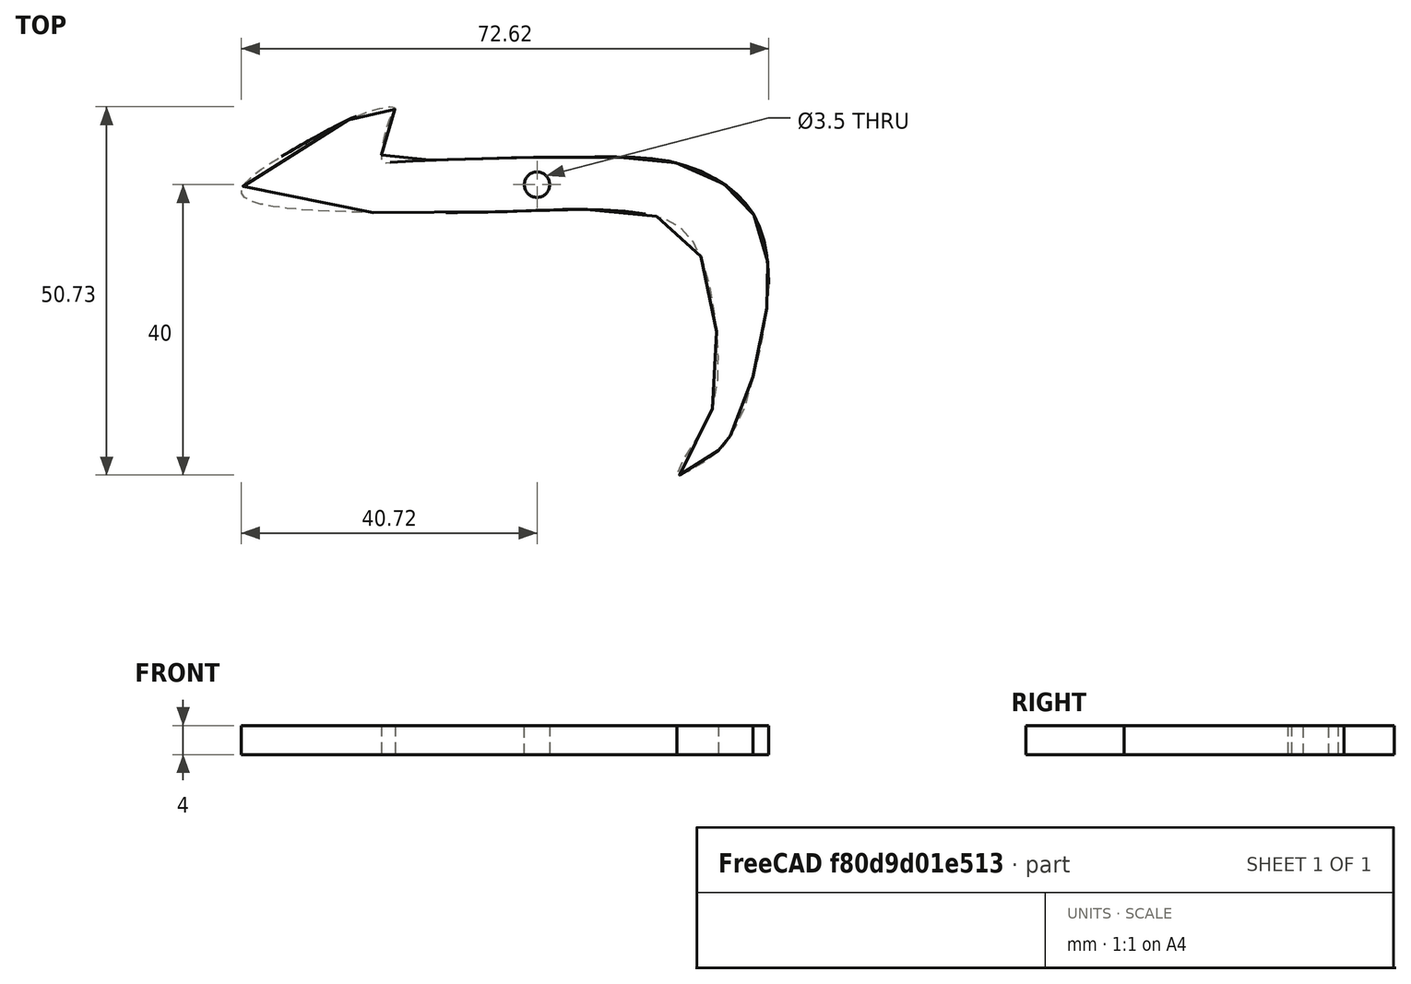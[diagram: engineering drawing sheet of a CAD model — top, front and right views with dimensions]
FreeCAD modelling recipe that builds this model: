
FCSTD DOCUMENT  (FreeCAD 1.0R39319 (Git))
Label: simple_trigger_V2
License: All rights reserved
LicenseURL: https://en.wikipedia.org/wiki/All_rights_reserved
objects: Sketcher::SketchObject×2, PartDesign::Pad×1, PartDesign::Plane×1, PartDesign::Pocket×1, PartDesign::Body×1
note: 12 computed .brp shape members not serialized (recipe doc carries the construction recipe); baked Part::Feature solids carry a one-line shape summary decoded from their .brp

FEATURE [Sketcher::SketchObject] Sketch
  ArcFitTolerance = 1e-06
  AttachmentSupport = -> [XY_Plane]
  FullyConstrained = false
  MakeInternals = false
  MapMode = 5
  sketch-geometry (77):
    g0-g38: Circle [constr] x39 (B-spline internal-alignment scaffolding for g39; pole/knot coordinates omitted)
    g39: BSplineCurve PolesCount=39 KnotsCount=37 Degree=3 IsPeriodic=0
    g40-g76: GeomPoint [constr] x37 (B-spline internal-alignment scaffolding for g39; pole/knot coordinates omitted)
  constraints (7):
    c: Weight(g0) = 1
    c: Equal(g0, g1-g38) x38
    c: InternalAlignment(g0-g38 -> g39) x39
    c: InternalAlignment(g40-g76 -> g39) x37
    c: PointOnObject(g4,g3)
    c: PointOnObject(g24,g23)
    c: Coincident(g38,g0)
FEATURE [PartDesign::Pad] Pad
  Direction = (0,0,1)
  Length = 4
  Length2 = 10
  Profile = -> Sketch
  ReferenceAxis = -> Sketch [N_Axis]
  Refine = true
  Suppressed = false
  Type = 0
FEATURE [PartDesign::Plane] DatumPlane
  AttachmentSupport = -> [Pad]
  Length = 60
  MapMode = 5
  Placement = pos=(0,0,4) rot=(0,0,1;0rad)
  ResizeMode = 0
  Width = 60
FEATURE [Sketcher::SketchObject] Sketch001
  ArcFitTolerance = 1e-06
  AttachmentSupport = -> [DatumPlane]
  FullyConstrained = true
  MakeInternals = false
  MapMode = 5
  Placement = pos=(0,0,4) rot=(0,0,1;0rad)
  sketch-geometry (1):
    g0: Circle CenterX=20 CenterY=39.5 CenterZ=0 NormalX=0 NormalY=0 NormalZ=1 AngleXU=0 Radius=1.75
  constraints (3):
    c: Diameter(g0) = 3.5
    c: DistanceY(g-1,g0) = 39.5
    c: DistanceX(g-1,g0) = 20
FEATURE [PartDesign::Pocket] Pocket
  BaseFeature = -> Pad
  Direction = (0,0,-1)
  Length = 5
  Length2 = 5
  Profile = -> Sketch001
  ReferenceAxis = -> Sketch001 [N_Axis]
  Refine = true
  Suppressed = false
  Type = 0
FEATURE [PartDesign::Body] Body
  AllowCompound = false
  Group = -> [Sketch,Pad,DatumPlane,Sketch001,Pocket]
  Origin = -> Origin
  Tip = -> Pocket
